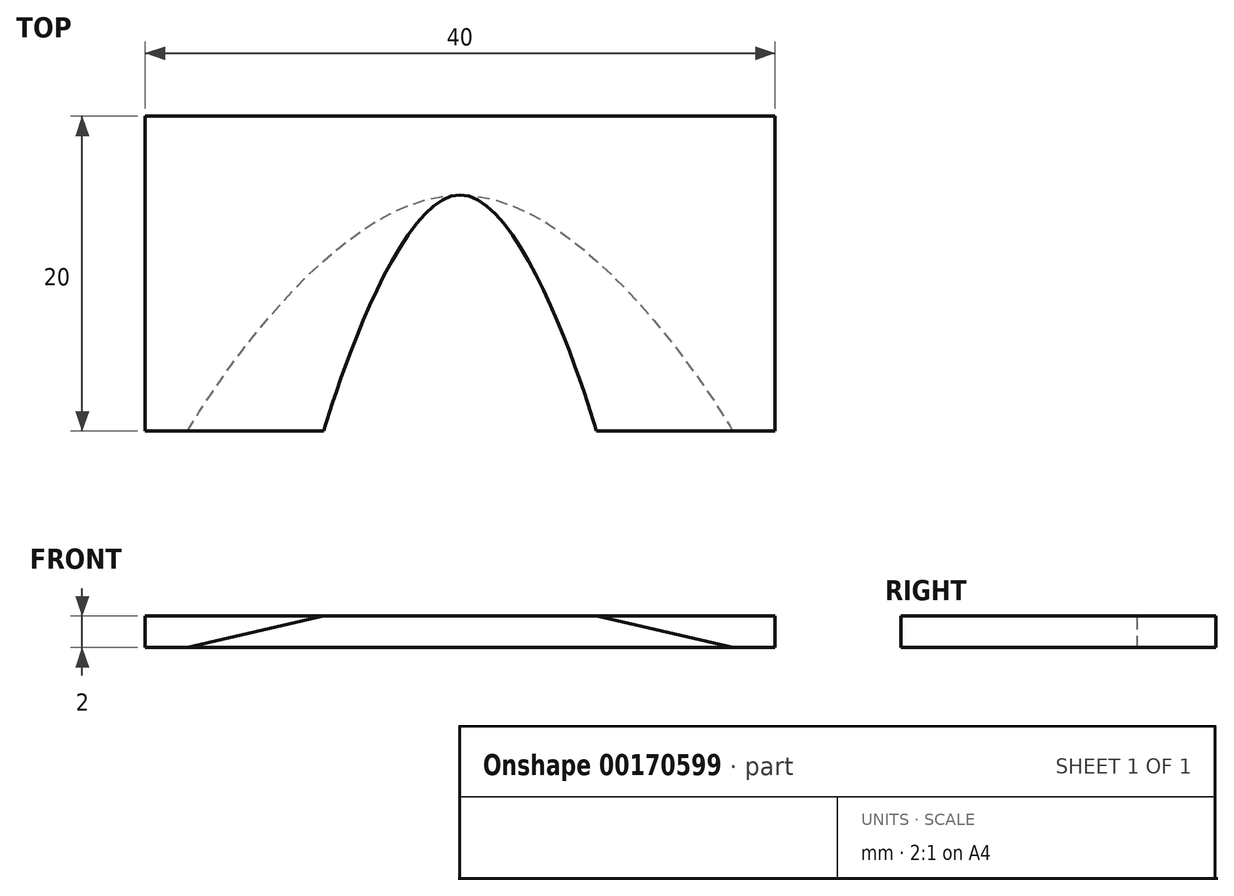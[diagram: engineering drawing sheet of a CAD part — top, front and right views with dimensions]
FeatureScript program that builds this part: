
annotation { "Feature Type Name" : "Feature", "Feature Type Description" : "" }
export const myFeature = defineFeature(function(context is Context, id is Id, definition is map)
    precondition{}
    {
        {
            assignVariable(context, id + "F0", {"name" : "Height", "anyValue" : 2});
        }
        {
            var Q0;
            Q0=qCreatedBy(makeId("Top.planeOp"),FACE);
            var sketch = newSketch(context, id + "F1", { "sketchPlane" : qUnion([Q0])});
            skLineSegment(sketch, "E0.bottom", {"start": v(-2.68, 0) * mm, "end": v(37.32, 0) * mm});
            skLineSegment(sketch, "E0.top", {"start": v(-2.68, 20) * mm, "end": v(37.32, 20) * mm});
            skLineSegment(sketch, "E0.left", {"start": v(-2.68, 0) * mm, "end": v(-2.68, 20) * mm});
            skLineSegment(sketch, "E0.right", {"start": v(37.32, 0) * mm, "end": v(37.32, 20) * mm});
            skSolve(sketch);
        }
        {
            var Q0;
            Q0 = qSketchRegion(id + "F1", true);
            extrude(context, id + "F2", {"entities" : qUnion([Q0]), "depth" : (getVariable(context, 'Height')) * mm});
        }
        {
            var Q0;
            Q0=qCreatedBy(makeId("Top.planeOp"),FACE);
            var sketch = newSketch(context, id + "F3", { "sketchPlane" : qUnion([Q0])});
            skLineSegment(sketch, "E1", {"start": v(0, 0) * mm, "end": v(34.64, 0) * mm});
            skFitSpline(sketch, "E2", {"points": [v(0, 0) * mm, v(17.32, 15) * mm, v(34.64, 0) * mm], "startDerivative": vector(0, 0.01) * mm, "endDerivative": vector(0, -0.01) * mm});
            skSolve(sketch);
        }
        {
            var Q0;
            Q0=qCreatedBy(makeId("Top.planeOp"),FACE);
            cPlane(context, id + "F4", {"entities" : qUnion([Q0]), "cplaneType" : CPlaneType.OFFSET, "offset" : (getVariable(context, 'Height')) * mm, "width" : 150 * mm, "height" : 150 * mm});
        }
        {
            var Q0;
            Q0=qCreatedBy(id+"F4.planeOp",FACE);
            var sketch = newSketch(context, id + "F5", { "sketchPlane" : qUnion([Q0])});
            skLineSegment(sketch, "E3", {"start": v(8.66, 0) * mm, "end": v(25.98, 0) * mm});
            skFitSpline(sketch, "E4", {"points": [v(8.66, 0) * mm, v(17.32, 15) * mm, v(25.98, 0) * mm], "startDerivative": vector(0, 0.01) * mm, "endDerivative": vector(0, -0.01) * mm});
            skSolve(sketch);
        }
        {
            var Q1;
            Q1=makeQuery(id+"F3.imprint","IMPRINT",FACE,{"disambiguationData":[TD([[makeQuery(id+"F3.imprint","IMPRINT",EDGE,{"derivedFrom":sQuery(id+"F3.wireOp",EDGE,"E1")}),1.0]])]});
            var Q2;
            Q2=qSketchRegion(id+"F5",true);
            loft(context, id + "F6", {"operationType" : NewBodyOperationType.REMOVE, "sheetProfilesArray" : [{ "sheetProfileEntities" : qUnion([Q1]) }, { "sheetProfileEntities" : qUnion([Q2]) }]});
        }
    });
